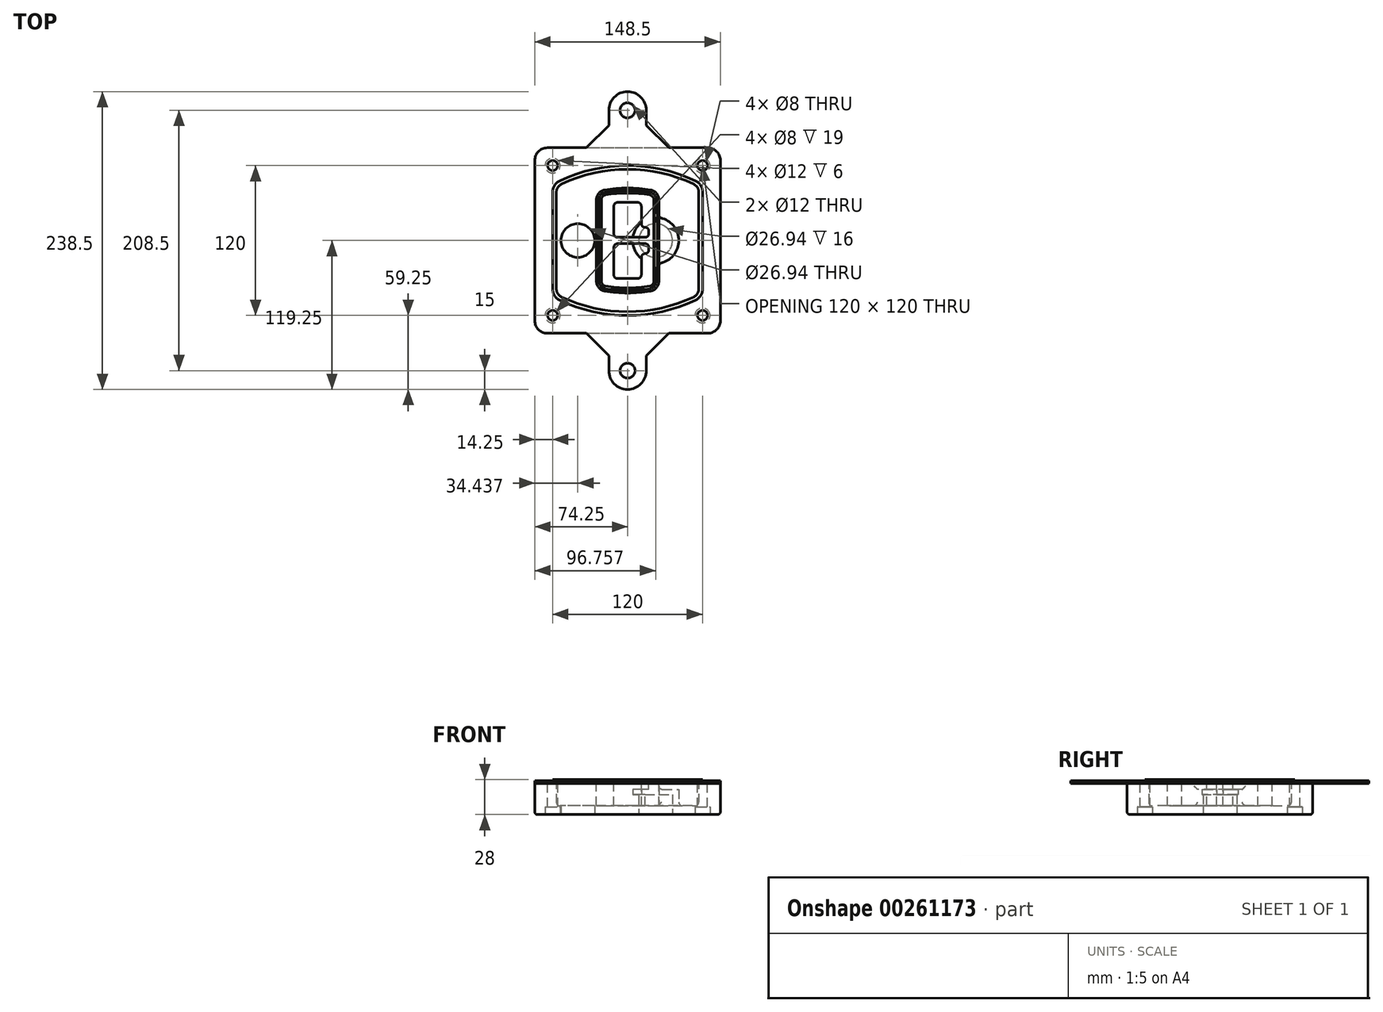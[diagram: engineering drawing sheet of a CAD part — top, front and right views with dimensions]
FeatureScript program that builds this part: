
annotation { "Feature Type Name" : "Feature", "Feature Type Description" : "" }
export const myFeature = defineFeature(function(context is Context, id is Id, definition is map)
    precondition{}
    {
        {
            var Q0;
            Q0=qCreatedBy(makeId("Top.planeOp"),FACE);
            var sketch = newSketch(context, id + "F0", { "sketchPlane" : qUnion([Q0])});
            skPoint(sketch, "E0.rect.middle", {"position": v(0, 0) * mm});
            skLineSegment(sketch, "E1.bottom", {"start": v(-64.25, -74.25) * mm, "end": v(64.25, -74.25) * mm});
            skLineSegment(sketch, "E1.top", {"start": v(-64.25, 74.25) * mm, "end": v(64.25, 74.25) * mm});
            skLineSegment(sketch, "E1.left", {"start": v(-74.25, -64.25) * mm, "end": v(-74.25, 64.25) * mm});
            skLineSegment(sketch, "E1.right", {"start": v(74.25, -64.25) * mm, "end": v(74.25, 64.25) * mm});
            skLineSegment(sketch, "E2", {"start": v(-74.25, 74.25) * mm, "end": v(74.25, -74.25) * mm, "construction": true});
            skLineSegment(sketch, "E3", {"start": v(74.25, 74.25) * mm, "end": v(-74.25, -74.25) * mm, "construction": true});
            skCircle(sketch, "E4", {"center": v(-60, 60) * mm, "radius": 4 * mm});
            skCircle(sketch, "E5", {"center": v(60, 60) * mm, "radius": 4 * mm});
            skCircle(sketch, "E6", {"center": v(60, -60) * mm, "radius": 4 * mm});
            skCircle(sketch, "E7", {"center": v(-60, -60) * mm, "radius": 4 * mm});
            skLineSegment(sketch, "E8", {"start": v(-60, 60) * mm, "end": v(60, 60) * mm, "construction": true});
            skLineSegment(sketch, "E9", {"start": v(60, 60) * mm, "end": v(60, -60) * mm, "construction": true});
            skLineSegment(sketch, "E10", {"start": v(60, -60) * mm, "end": v(-60, -60) * mm, "construction": true});
            skLineSegment(sketch, "E11", {"start": v(-60, -60) * mm, "end": v(-60, 60) * mm, "construction": true});
            skLineSegment(sketch, "E12", {"start": v(-60, 38.83) * mm, "end": v(-60, -38.83) * mm});
            skLineSegment(sketch, "E13", {"start": v(60, 38.83) * mm, "end": v(60, -38.83) * mm});
            skArc(sketch, "E14", {"start": v(54.26, 47.88) * mm, "mid": v(0, 60) * mm, "end": v(-54.26, 47.88) * mm});
            skArc(sketch, "E15", {"start": v(-54.26, -47.88) * mm, "mid": v(0, -60) * mm, "end": v(54.26, -47.88) * mm});
            skLineSegment(sketch, "E16", {"start": v(-60, 0) * mm, "end": v(60, 0) * mm, "construction": true});
            skPoint(sketch, "E17.visualSharp", {"position": v(-60, -45) * mm});
            skArc(sketch, "E17.filletArc", {"start": v(-60, -38.83) * mm, "mid": v(-58.44, -44.2) * mm, "end": v(-54.26, -47.88) * mm});
            skPoint(sketch, "E18.visualSharp", {"position": v(-60, 45) * mm});
            skArc(sketch, "E18.filletArc", {"start": v(-54.26, 47.88) * mm, "mid": v(-58.44, 44.2) * mm, "end": v(-60, 38.83) * mm});
            skPoint(sketch, "E19.visualSharp", {"position": v(60, 45) * mm});
            skArc(sketch, "E19.filletArc", {"start": v(60, 38.83) * mm, "mid": v(58.44, 44.2) * mm, "end": v(54.26, 47.88) * mm});
            skPoint(sketch, "E20.visualSharp", {"position": v(60, -45) * mm});
            skArc(sketch, "E20.filletArc", {"start": v(54.26, -47.88) * mm, "mid": v(58.44, -44.2) * mm, "end": v(60, -38.83) * mm});
            skPoint(sketch, "E21.visualSharp", {"position": v(-74.25, 74.25) * mm});
            skArc(sketch, "E21.filletArc", {"start": v(-64.25, 74.25) * mm, "mid": v(-71.32, 71.32) * mm, "end": v(-74.25, 64.25) * mm});
            skPoint(sketch, "E22.visualSharp", {"position": v(74.25, 74.25) * mm});
            skArc(sketch, "E22.filletArc", {"start": v(74.25, 64.25) * mm, "mid": v(71.32, 71.32) * mm, "end": v(64.25, 74.25) * mm});
            skPoint(sketch, "E23.visualSharp", {"position": v(74.25, -74.25) * mm});
            skArc(sketch, "E23.filletArc", {"start": v(64.25, -74.25) * mm, "mid": v(71.32, -71.32) * mm, "end": v(74.25, -64.25) * mm});
            skPoint(sketch, "E24.visualSharp", {"position": v(-74.25, -74.25) * mm});
            skArc(sketch, "E24.filletArc", {"start": v(-74.25, -64.25) * mm, "mid": v(-71.32, -71.32) * mm, "end": v(-64.25, -74.25) * mm});
            skArc(sketch, "E25.0", {"start": v(57, 38.83) * mm, "mid": v(55.9, 42.58) * mm, "end": v(52.98, 45.17) * mm});
            skLineSegment(sketch, "E25.1", {"start": v(57, 38.83) * mm, "end": v(57, -38.83) * mm});
            skArc(sketch, "E25.2", {"start": v(52.98, -45.17) * mm, "mid": v(55.9, -42.58) * mm, "end": v(57, -38.83) * mm});
            skArc(sketch, "E25.3", {"start": v(-52.98, -45.17) * mm, "mid": v(0, -57) * mm, "end": v(52.98, -45.17) * mm});
            skArc(sketch, "E25.4", {"start": v(-57, -38.83) * mm, "mid": v(-55.9, -42.58) * mm, "end": v(-52.98, -45.17) * mm});
            skArc(sketch, "E25.5", {"start": v(52.98, 45.17) * mm, "mid": v(0, 57) * mm, "end": v(-52.98, 45.17) * mm});
            skLineSegment(sketch, "E25.6", {"start": v(-57, 38.83) * mm, "end": v(-57, -38.83) * mm});
            skArc(sketch, "E25.7", {"start": v(-52.98, 45.17) * mm, "mid": v(-55.9, 42.58) * mm, "end": v(-57, 38.83) * mm});
            skArc(sketch, "E26.0", {"start": v(-55.96, 51.5) * mm, "mid": v(-61.82, 46.33) * mm, "end": v(-64, 38.83) * mm});
            skArc(sketch, "E26.1", {"start": v(55.96, 51.5) * mm, "mid": v(0, 64) * mm, "end": v(-55.96, 51.5) * mm});
            skArc(sketch, "E26.2", {"start": v(64, 38.83) * mm, "mid": v(61.82, 46.33) * mm, "end": v(55.96, 51.5) * mm});
            skLineSegment(sketch, "E26.3", {"start": v(64, 38.83) * mm, "end": v(64, -38.83) * mm});
            skArc(sketch, "E26.4", {"start": v(55.96, -51.5) * mm, "mid": v(61.82, -46.33) * mm, "end": v(64, -38.83) * mm});
            skLineSegment(sketch, "E26.5", {"start": v(-64, 38.83) * mm, "end": v(-64, -38.83) * mm});
            skArc(sketch, "E26.6", {"start": v(-55.96, -51.5) * mm, "mid": v(0, -64) * mm, "end": v(55.96, -51.5) * mm});
            skArc(sketch, "E26.7", {"start": v(-64, -38.83) * mm, "mid": v(-61.82, -46.33) * mm, "end": v(-55.96, -51.5) * mm});
            skSolve(sketch);
        }
        {
            var Q0;
            Q0=makeQuery(id+"F0.imprint","IMPRINT",FACE,{"disambiguationData":[TD([[makeQuery(id+"F0.imprint","IMPRINT",EDGE,{"derivedFrom":sQuery(id+"F0.wireOp",EDGE,"E1.bottom")}),1.0]])]});
            var Q1;
            Q1=makeQuery(id+"F0.imprint","IMPRINT",FACE,{"disambiguationData":[TD([[makeQuery(id+"F0.imprint","IMPRINT",EDGE,{"derivedFrom":sQuery(id+"F0.wireOp",EDGE,"E12")}),1.0]])]});
            var Q2;
            Q2=makeQuery(id+"F0.imprint","IMPRINT",FACE,{"disambiguationData":[TD([[makeQuery(id+"F0.imprint","IMPRINT",EDGE,{"derivedFrom":sQuery(id+"F0.wireOp",EDGE,"E25.0")}),1.0]])]});
            var Q3;
            Q3=makeQuery(id+"F0.imprint","IMPRINT",FACE,{"disambiguationData":[TD([[makeQuery(id+"F0.imprint","IMPRINT",EDGE,{"derivedFrom":sQuery(id+"F0.wireOp",EDGE,"E12")}),-1.0]])]});
            extrude(context, id + "F1", {"entities" : qUnion([Q0, Q1, Q2, Q3]), "oppositeDirection" : true, "depth" : 25 * mm});
        }
        {
            var Q0;
            Q0=makeQuery(id+"F0.imprint","IMPRINT",FACE,{"disambiguationData":[TD([[makeQuery(id+"F0.imprint","IMPRINT",EDGE,{"derivedFrom":sQuery(id+"F0.wireOp",EDGE,"E12")}),1.0]])]});
            extrude(context, id + "F2", {"entities" : qUnion([Q0]), "operationType" : NewBodyOperationType.ADD, "depth" : 3 * mm});
        }
        {
            var Q0;
            Q0=makeQuery(id+"F0.imprint","IMPRINT",FACE,{"disambiguationData":[TD([[makeQuery(id+"F0.imprint","IMPRINT",EDGE,{"derivedFrom":sQuery(id+"F0.wireOp",EDGE,"E25.0")}),1.0]])]});
            extrude(context, id + "F3", {"entities" : qUnion([Q0]), "operationType" : NewBodyOperationType.REMOVE, "oppositeDirection" : true, "depth" : 18 * mm});
        }
        {
            var Q0;
            Q0=makeQuery(id+"F2.opExtrude","CAP_FACE",FACE,{"disambiguationData":[OSD([sQuery(id+"F0.wireOp",EDGE,"E12"),sQuery(id+"F0.wireOp",EDGE,"E13"),sQuery(id+"F0.wireOp",EDGE,"E14"),sQuery(id+"F0.wireOp",EDGE,"E15"),sQuery(id+"F0.wireOp",EDGE,"E17.filletArc"),sQuery(id+"F0.wireOp",EDGE,"E18.filletArc"),sQuery(id+"F0.wireOp",EDGE,"E19.filletArc"),sQuery(id+"F0.wireOp",EDGE,"E20.filletArc"),sQuery(id+"F0.wireOp",EDGE,"E25.0"),sQuery(id+"F0.wireOp",EDGE,"E25.1"),sQuery(id+"F0.wireOp",EDGE,"E25.2"),sQuery(id+"F0.wireOp",EDGE,"E25.3"),sQuery(id+"F0.wireOp",EDGE,"E25.4"),sQuery(id+"F0.wireOp",EDGE,"E25.5"),sQuery(id+"F0.wireOp",EDGE,"E25.6"),sQuery(id+"F0.wireOp",EDGE,"E25.7")])],"isStart":false});
            var sketch = newSketch(context, id + "F4", { "sketchPlane" : qUnion([Q0])});
            skArc(sketch, "E27.0", {"start": v(-18.34, -40.45) * mm, "mid": v(0, -42) * mm, "end": v(18.34, -40.45) * mm});
            skArc(sketch, "E28.0", {"start": v(18.34, 40.45) * mm, "mid": v(0, 42) * mm, "end": v(-18.34, 40.45) * mm});
            skLineSegment(sketch, "E29", {"start": v(-25, 32.57) * mm, "end": v(-25, -32.57) * mm});
            skLineSegment(sketch, "E30", {"start": v(25, 32.57) * mm, "end": v(25, -32.57) * mm});
            skLineSegment(sketch, "E31", {"start": v(-25, 39.1) * mm, "end": v(25, 39.1) * mm, "construction": true});
            skLineSegment(sketch, "E32", {"start": v(-25, -39.1) * mm, "end": v(25, -39.1) * mm, "construction": true});
            skPoint(sketch, "E33.visualSharp", {"position": v(-25, 39.1) * mm});
            skArc(sketch, "E33.filletArc", {"start": v(-18.34, 40.45) * mm, "mid": v(-23.11, 37.73) * mm, "end": v(-25, 32.57) * mm});
            skPoint(sketch, "E34.visualSharp", {"position": v(25, 39.1) * mm});
            skArc(sketch, "E34.filletArc", {"start": v(25, 32.57) * mm, "mid": v(23.11, 37.73) * mm, "end": v(18.34, 40.45) * mm});
            skPoint(sketch, "E35.visualSharp", {"position": v(25, -39.1) * mm});
            skArc(sketch, "E35.filletArc", {"start": v(18.34, -40.45) * mm, "mid": v(23.11, -37.73) * mm, "end": v(25, -32.57) * mm});
            skPoint(sketch, "E36.visualSharp", {"position": v(-25, -39.1) * mm});
            skArc(sketch, "E36.filletArc", {"start": v(-25, -32.57) * mm, "mid": v(-23.11, -37.73) * mm, "end": v(-18.34, -40.45) * mm});
            skArc(sketch, "E37.0", {"start": v(52.98, 45.17) * mm, "mid": v(0, 57) * mm, "end": v(-52.98, 45.17) * mm});
            skArc(sketch, "E37.1", {"start": v(-52.98, 45.17) * mm, "mid": v(-55.9, 42.58) * mm, "end": v(-57, 38.83) * mm});
            skLineSegment(sketch, "E37.2", {"start": v(-57, 38.83) * mm, "end": v(-57, -38.83) * mm});
            skArc(sketch, "E37.3", {"start": v(-57, -38.83) * mm, "mid": v(-55.9, -42.58) * mm, "end": v(-52.98, -45.17) * mm});
            skArc(sketch, "E37.4", {"start": v(-52.98, -45.17) * mm, "mid": v(0, -57) * mm, "end": v(52.98, -45.17) * mm});
            skArc(sketch, "E37.5", {"start": v(52.98, -45.17) * mm, "mid": v(55.9, -42.58) * mm, "end": v(57, -38.83) * mm});
            skLineSegment(sketch, "E37.6", {"start": v(57, 38.83) * mm, "end": v(57, -38.83) * mm});
            skArc(sketch, "E37.7", {"start": v(57, 38.83) * mm, "mid": v(55.9, 42.58) * mm, "end": v(52.98, 45.17) * mm});
            skLineSegment(sketch, "E38.0", {"start": v(23, 32.57) * mm, "end": v(23, -32.57) * mm});
            skArc(sketch, "E38.1", {"start": v(18, -38.48) * mm, "mid": v(21.58, -36.44) * mm, "end": v(23, -32.57) * mm});
            skArc(sketch, "E38.2", {"start": v(-18, -38.48) * mm, "mid": v(0, -40) * mm, "end": v(18, -38.48) * mm});
            skArc(sketch, "E38.3", {"start": v(-23, -32.57) * mm, "mid": v(-21.58, -36.44) * mm, "end": v(-18, -38.48) * mm});
            skLineSegment(sketch, "E38.4", {"start": v(-23, 32.57) * mm, "end": v(-23, -32.57) * mm});
            skArc(sketch, "E38.5", {"start": v(23, 32.57) * mm, "mid": v(21.58, 36.44) * mm, "end": v(18, 38.48) * mm});
            skArc(sketch, "E38.6", {"start": v(-18, 38.48) * mm, "mid": v(-21.58, 36.44) * mm, "end": v(-23, 32.57) * mm});
            skArc(sketch, "E38.7", {"start": v(18, 38.48) * mm, "mid": v(0, 40) * mm, "end": v(-18, 38.48) * mm});
            skArc(sketch, "E39.0", {"start": v(21, 32.57) * mm, "mid": v(20.06, 35.15) * mm, "end": v(17.67, 36.5) * mm});
            skLineSegment(sketch, "E39.1", {"start": v(21, 32.57) * mm, "end": v(21, -32.57) * mm});
            skArc(sketch, "E39.2", {"start": v(17.67, -36.5) * mm, "mid": v(20.06, -35.15) * mm, "end": v(21, -32.57) * mm});
            skArc(sketch, "E39.3", {"start": v(-17.67, -36.5) * mm, "mid": v(0, -38) * mm, "end": v(17.67, -36.5) * mm});
            skArc(sketch, "E39.4", {"start": v(-21, -32.57) * mm, "mid": v(-20.06, -35.15) * mm, "end": v(-17.67, -36.5) * mm});
            skArc(sketch, "E39.5", {"start": v(17.67, 36.5) * mm, "mid": v(0, 38) * mm, "end": v(-17.67, 36.5) * mm});
            skLineSegment(sketch, "E39.6", {"start": v(-21, 32.57) * mm, "end": v(-21, -32.57) * mm});
            skArc(sketch, "E39.7", {"start": v(-17.67, 36.5) * mm, "mid": v(-20.06, 35.15) * mm, "end": v(-21, 32.57) * mm});
            skLineSegment(sketch, "E40", {"start": v(-25, 0) * mm, "end": v(25, 0) * mm, "construction": true});
            skLineSegment(sketch, "E41", {"start": v(-11, 5.5) * mm, "end": v(-11, 27.5) * mm});
            skLineSegment(sketch, "E42", {"start": v(-8, 30.5) * mm, "end": v(8, 30.5) * mm});
            skLineSegment(sketch, "E43", {"start": v(11, 27.5) * mm, "end": v(11, 13.5) * mm});
            skLineSegment(sketch, "E44", {"start": v(14, 10.5) * mm, "end": v(14, 10.5) * mm});
            skLineSegment(sketch, "E45", {"start": v(17, 7.5) * mm, "end": v(17, 5.5) * mm});
            skLineSegment(sketch, "E46", {"start": v(14, 2.5) * mm, "end": v(-8, 2.5) * mm});
            skPoint(sketch, "E47.visualSharp", {"position": v(-11, 30.5) * mm});
            skArc(sketch, "E47.filletArc", {"start": v(-8, 30.5) * mm, "mid": v(-10.12, 29.62) * mm, "end": v(-11, 27.5) * mm});
            skPoint(sketch, "E48.visualSharp", {"position": v(11, 30.5) * mm});
            skArc(sketch, "E48.filletArc", {"start": v(11, 27.5) * mm, "mid": v(10.12, 29.62) * mm, "end": v(8, 30.5) * mm});
            skPoint(sketch, "E49.visualSharp", {"position": v(11, 10.5) * mm});
            skArc(sketch, "E49.filletArc", {"start": v(11, 13.5) * mm, "mid": v(11.88, 11.38) * mm, "end": v(14, 10.5) * mm});
            skPoint(sketch, "E50.visualSharp", {"position": v(17, 10.5) * mm});
            skArc(sketch, "E50.filletArc", {"start": v(17, 7.5) * mm, "mid": v(16.12, 9.62) * mm, "end": v(14, 10.5) * mm});
            skPoint(sketch, "E51.visualSharp", {"position": v(17, 2.5) * mm});
            skArc(sketch, "E51.filletArc", {"start": v(14, 2.5) * mm, "mid": v(16.12, 3.38) * mm, "end": v(17, 5.5) * mm});
            skPoint(sketch, "E52.visualSharp", {"position": v(-11, 2.5) * mm});
            skArc(sketch, "E52.filletArc", {"start": v(-11, 5.5) * mm, "mid": v(-10.12, 3.38) * mm, "end": v(-8, 2.5) * mm});
            skLineSegment(sketch, "E53.0.MirrorCS", {"start": v(14, -2.5) * mm, "end": v(-8, -2.5) * mm});
            skArc(sketch, "E54.0.MirrorCS", {"start": v(-11, -5.5) * mm, "mid": v(-10.12, -3.38) * mm, "end": v(-8, -2.5) * mm});
            skLineSegment(sketch, "E55.0.MirrorCS", {"start": v(-11, -5.5) * mm, "end": v(-11, -27.5) * mm});
            skArc(sketch, "E56.0.MirrorCS", {"start": v(-8, -30.5) * mm, "mid": v(-10.12, -29.62) * mm, "end": v(-11, -27.5) * mm});
            skLineSegment(sketch, "E57.0.MirrorCS", {"start": v(-8, -30.5) * mm, "end": v(8, -30.5) * mm});
            skArc(sketch, "E58.0.MirrorCS", {"start": v(11, -27.5) * mm, "mid": v(10.12, -29.62) * mm, "end": v(8, -30.5) * mm});
            skLineSegment(sketch, "E59.0.MirrorCS", {"start": v(11, -27.5) * mm, "end": v(11, -13.5) * mm});
            skArc(sketch, "E60.0.MirrorCS", {"start": v(11, -13.5) * mm, "mid": v(11.88, -11.38) * mm, "end": v(14, -10.5) * mm});
            skArc(sketch, "E61.0.MirrorCS", {"start": v(17, -7.5) * mm, "mid": v(16.12, -9.62) * mm, "end": v(14, -10.5) * mm});
            skLineSegment(sketch, "E62.0.MirrorCS", {"start": v(17, -7.5) * mm, "end": v(17, -5.5) * mm});
            skArc(sketch, "E63.0.MirrorCS", {"start": v(14, -2.5) * mm, "mid": v(16.12, -3.38) * mm, "end": v(17, -5.5) * mm});
            skSolve(sketch);
        }
        {
            var Q0;
            Q0=makeQuery(id+"F4.imprint","IMPRINT",FACE,{"disambiguationData":[TD([[makeQuery(id+"F4.imprint","IMPRINT",EDGE,{"derivedFrom":sQuery(id+"F4.wireOp",EDGE,"E27.0")}),1.0]])]});
            var Q1;
            Q1=makeQuery(id+"F4.imprint","IMPRINT",FACE,{"disambiguationData":[TD([[makeQuery(id+"F4.imprint","IMPRINT",EDGE,{"derivedFrom":sQuery(id+"F4.wireOp",EDGE,"E38.0")}),-1.0]])]});
            var Q2;
            Q2=makeQuery(id+"F4.imprint","IMPRINT",FACE,{"disambiguationData":[TD([[makeQuery(id+"F4.imprint","IMPRINT",EDGE,{"derivedFrom":sQuery(id+"F4.wireOp",EDGE,"E39.0")}),1.0]])]});
            extrude(context, id + "F5", {"entities" : qUnion([Q0, Q1, Q2]), "operationType" : NewBodyOperationType.ADD, "endBound" : BoundingType.UP_TO_NEXT, "oppositeDirection" : true, "depth" : 25 * mm});
        }
        {
            var Q0;
            Q0=makeQuery(id+"F4.imprint","IMPRINT",FACE,{"disambiguationData":[TD([[makeQuery(id+"F4.imprint","IMPRINT",EDGE,{"derivedFrom":sQuery(id+"F4.wireOp",EDGE,"E38.0")}),-1.0]])]});
            extrude(context, id + "F6", {"entities" : qUnion([Q0]), "operationType" : NewBodyOperationType.REMOVE, "oppositeDirection" : true, "depth" : 2 * mm});
        }
        {
            var Q0;
            Q0=makeQuery(id+"F1.opExtrude","CAP_FACE",FACE,{"disambiguationData":[OSD([sQuery(id+"F0.wireOp",EDGE,"E1.bottom"),sQuery(id+"F0.wireOp",EDGE,"E1.top"),sQuery(id+"F0.wireOp",EDGE,"E1.left"),sQuery(id+"F0.wireOp",EDGE,"E1.right"),sQuery(id+"F0.wireOp",EDGE,"E4"),sQuery(id+"F0.wireOp",EDGE,"E5"),sQuery(id+"F0.wireOp",EDGE,"E6"),sQuery(id+"F0.wireOp",EDGE,"E7"),sQuery(id+"F0.wireOp",EDGE,"E21.filletArc"),sQuery(id+"F0.wireOp",EDGE,"E22.filletArc"),sQuery(id+"F0.wireOp",EDGE,"E23.filletArc"),sQuery(id+"F0.wireOp",EDGE,"E24.filletArc")])],"isStart":false});
            var sketch = newSketch(context, id + "F7", { "sketchPlane" : qUnion([Q0])});
            skCircle(sketch, "E64", {"center": v(22.5, 0) * mm, "radius": 13.47 * mm});
            skCircle(sketch, "E65", {"center": v(-39.81, 0) * mm, "radius": 13.47 * mm});
            skLineSegment(sketch, "E66", {"start": v(74.25, 0) * mm, "end": v(-74.25, 0) * mm});
            skCircle(sketch, "E67", {"center": v(22.5, 0) * mm, "radius": 18.47 * mm});
            skCircle(sketch, "E68", {"center": v(60, -60) * mm, "radius": 6 * mm});
            skCircle(sketch, "E69", {"center": v(-60, -60) * mm, "radius": 6 * mm});
            skCircle(sketch, "E70", {"center": v(-60, 60) * mm, "radius": 6 * mm});
            skCircle(sketch, "E71", {"center": v(60, 60) * mm, "radius": 6 * mm});
            skSolve(sketch);
        }
        {
            var Q0;
            {var subQ1=sQuery(id+"F7.wireOp",EDGE,"E66");var subQ4=sQuery(id+"F7.wireOp",EDGE,"E64");var subQ6=makeQuery(id+"F7.imprint","INTERSECT",VERTEX,{"disambiguationData":[OD(0.0)],"derivedFrom":[subQ4,subQ1]});Q0=makeQuery(id+"F7.imprint","IMPRINT",FACE,{"disambiguationData":[TD([[makeQuery(id+"F7.imprint","IMPRINT",EDGE,{"disambiguationData":[TD([[subQ6,-1.0]])],"derivedFrom":subQ4}),-1.0]])]});}
            var Q1;
            {var subQ0=sQuery(id+"F7.wireOp",EDGE,"E66");var subQ1=sQuery(id+"F7.wireOp",EDGE,"E64");var subQ3=makeQuery(id+"F7.imprint","INTERSECT",VERTEX,{"disambiguationData":[OD(0.0)],"derivedFrom":[subQ1,subQ0]});Q1=makeQuery(id+"F7.imprint","IMPRINT",FACE,{"disambiguationData":[TD([[makeQuery(id+"F7.imprint","IMPRINT",EDGE,{"disambiguationData":[TD([[subQ3,-1.0]])],"derivedFrom":subQ1}),1.0]])]});}
            var Q2;
            {var subQ0=sQuery(id+"F7.wireOp",EDGE,"E66");var subQ1=sQuery(id+"F7.wireOp",EDGE,"E64");var subQ3=makeQuery(id+"F7.imprint","INTERSECT",VERTEX,{"disambiguationData":[OD(0.0)],"derivedFrom":[subQ1,subQ0]});Q2=makeQuery(id+"F7.imprint","IMPRINT",FACE,{"disambiguationData":[TD([[makeQuery(id+"F7.imprint","IMPRINT",EDGE,{"disambiguationData":[TD([[subQ3,1.0]])],"derivedFrom":subQ1}),1.0]])]});}
            var Q3;
            {var subQ1=sQuery(id+"F7.wireOp",EDGE,"E66");var subQ4=sQuery(id+"F7.wireOp",EDGE,"E64");var subQ6=makeQuery(id+"F7.imprint","INTERSECT",VERTEX,{"disambiguationData":[OD(0.0)],"derivedFrom":[subQ4,subQ1]});Q3=makeQuery(id+"F7.imprint","IMPRINT",FACE,{"disambiguationData":[TD([[makeQuery(id+"F7.imprint","IMPRINT",EDGE,{"disambiguationData":[TD([[subQ6,1.0]])],"derivedFrom":subQ4}),-1.0]])]});}
            extrude(context, id + "F8", {"entities" : qUnion([Q0, Q1, Q2, Q3]), "operationType" : NewBodyOperationType.ADD, "oppositeDirection" : true, "depth" : 20 * mm});
        }
        {
            var Q0;
            {var subQ0=sQuery(id+"F7.wireOp",EDGE,"E66");var subQ1=sQuery(id+"F7.wireOp",EDGE,"E64");var subQ3=makeQuery(id+"F7.imprint","INTERSECT",VERTEX,{"disambiguationData":[OD(0.0)],"derivedFrom":[subQ1,subQ0]});Q0=makeQuery(id+"F7.imprint","IMPRINT",FACE,{"disambiguationData":[TD([[makeQuery(id+"F7.imprint","IMPRINT",EDGE,{"disambiguationData":[TD([[subQ3,-1.0]])],"derivedFrom":subQ1}),1.0]])]});}
            var Q1;
            {var subQ0=sQuery(id+"F7.wireOp",EDGE,"E66");var subQ1=sQuery(id+"F7.wireOp",EDGE,"E64");var subQ3=makeQuery(id+"F7.imprint","INTERSECT",VERTEX,{"disambiguationData":[OD(0.0)],"derivedFrom":[subQ1,subQ0]});Q1=makeQuery(id+"F7.imprint","IMPRINT",FACE,{"disambiguationData":[TD([[makeQuery(id+"F7.imprint","IMPRINT",EDGE,{"disambiguationData":[TD([[subQ3,1.0]])],"derivedFrom":subQ1}),1.0]])]});}
            extrude(context, id + "F9", {"entities" : qUnion([Q0, Q1]), "operationType" : NewBodyOperationType.REMOVE, "oppositeDirection" : true, "depth" : 16 * mm});
        }
        {
            var Q0;
            {var subQ0=sQuery(id+"F7.wireOp",EDGE,"E66");var subQ1=sQuery(id+"F7.wireOp",EDGE,"E65");var subQ3=makeQuery(id+"F7.imprint","INTERSECT",VERTEX,{"disambiguationData":[OD(0.0)],"derivedFrom":[subQ1,subQ0]});Q0=makeQuery(id+"F7.imprint","IMPRINT",FACE,{"disambiguationData":[TD([[makeQuery(id+"F7.imprint","IMPRINT",EDGE,{"disambiguationData":[TD([[subQ3,-1.0]])],"derivedFrom":subQ1}),1.0]])]});}
            var Q1;
            {var subQ0=sQuery(id+"F7.wireOp",EDGE,"E66");var subQ1=sQuery(id+"F7.wireOp",EDGE,"E65");var subQ3=makeQuery(id+"F7.imprint","INTERSECT",VERTEX,{"disambiguationData":[OD(0.0)],"derivedFrom":[subQ1,subQ0]});Q1=makeQuery(id+"F7.imprint","IMPRINT",FACE,{"disambiguationData":[TD([[makeQuery(id+"F7.imprint","IMPRINT",EDGE,{"disambiguationData":[TD([[subQ3,1.0]])],"derivedFrom":subQ1}),1.0]])]});}
            extrude(context, id + "F10", {"entities" : qUnion([Q0, Q1]), "operationType" : NewBodyOperationType.REMOVE, "oppositeDirection" : true, "depth" : 25 * mm});
        }
        {
            var Q0;
            Q0=makeQuery(id+"F7.imprint","IMPRINT",FACE,{"disambiguationData":[TD([[makeQuery(id+"F7.imprint","IMPRINT",EDGE,{"derivedFrom":sQuery(id+"F7.wireOp",EDGE,"E68")}),1.0]])]});
            var Q1;
            Q1=makeQuery(id+"F7.imprint","IMPRINT",FACE,{"disambiguationData":[TD([[makeQuery(id+"F7.imprint","IMPRINT",EDGE,{"derivedFrom":makeQuery(id+"F1.opExtrude","CAP_EDGE",EDGE,{"disambiguationData":[OSD([sQuery(id+"F0.wireOp",EDGE,"E5")])],"isStart":false})}),-1.0]])]});
            var Q2;
            Q2=makeQuery(id+"F7.imprint","IMPRINT",FACE,{"disambiguationData":[TD([[makeQuery(id+"F7.imprint","IMPRINT",EDGE,{"derivedFrom":sQuery(id+"F7.wireOp",EDGE,"E69")}),1.0]])]});
            var Q3;
            Q3=makeQuery(id+"F7.imprint","IMPRINT",FACE,{"disambiguationData":[TD([[makeQuery(id+"F7.imprint","IMPRINT",EDGE,{"derivedFrom":makeQuery(id+"F1.opExtrude","CAP_EDGE",EDGE,{"disambiguationData":[OSD([sQuery(id+"F0.wireOp",EDGE,"E4")])],"isStart":false})}),-1.0]])]});
            var Q4;
            Q4=makeQuery(id+"F7.imprint","IMPRINT",FACE,{"disambiguationData":[TD([[makeQuery(id+"F7.imprint","IMPRINT",EDGE,{"derivedFrom":sQuery(id+"F7.wireOp",EDGE,"E70")}),1.0]])]});
            var Q5;
            Q5=makeQuery(id+"F7.imprint","IMPRINT",FACE,{"disambiguationData":[TD([[makeQuery(id+"F7.imprint","IMPRINT",EDGE,{"derivedFrom":makeQuery(id+"F1.opExtrude","CAP_EDGE",EDGE,{"disambiguationData":[OSD([sQuery(id+"F0.wireOp",EDGE,"E7")])],"isStart":false})}),-1.0]])]});
            var Q6;
            Q6=makeQuery(id+"F7.imprint","IMPRINT",FACE,{"disambiguationData":[TD([[makeQuery(id+"F7.imprint","IMPRINT",EDGE,{"derivedFrom":sQuery(id+"F7.wireOp",EDGE,"E71")}),1.0]])]});
            var Q7;
            Q7=makeQuery(id+"F7.imprint","IMPRINT",FACE,{"disambiguationData":[TD([[makeQuery(id+"F7.imprint","IMPRINT",EDGE,{"derivedFrom":makeQuery(id+"F1.opExtrude","CAP_EDGE",EDGE,{"disambiguationData":[OSD([sQuery(id+"F0.wireOp",EDGE,"E6")])],"isStart":false})}),-1.0]])]});
            extrude(context, id + "F11", {"entities" : qUnion([Q0, Q1, Q2, Q3, Q4, Q5, Q6, Q7]), "operationType" : NewBodyOperationType.REMOVE, "oppositeDirection" : true, "depth" : 6 * mm});
        }
        {
            var Q0;
            Q0=makeQuery(id+"F9.boolean.opBoolean","COPY",FACE,{"derivedFrom":makeQuery(id+"F9.opExtrude","CAP_FACE",FACE,{"disambiguationData":[OSD([sQuery(id+"F7.wireOp",EDGE,"E64")])],"isStart":false})});
            var sketch = newSketch(context, id + "F12", { "sketchPlane" : qUnion([Q0])});
            skArc(sketch, "E72.0", {"start": v(11, 14.45) * mm, "mid": v(6.45, 9.13) * mm, "end": v(4.2, 2.5) * mm});
            skArc(sketch, "E72.1", {"start": v(4.2, -2.5) * mm, "mid": v(6.45, -9.13) * mm, "end": v(11, -14.45) * mm});
            skLineSegment(sketch, "E73", {"start": v(4.2, -2.5) * mm, "end": v(14, -2.5) * mm});
            skLineSegment(sketch, "E74.0", {"start": v(14, 2.5) * mm, "end": v(4.2, 2.5) * mm});
            skArc(sketch, "E74.1", {"start": v(14, 2.5) * mm, "mid": v(16.12, 3.38) * mm, "end": v(17, 5.5) * mm});
            skLineSegment(sketch, "E74.2", {"start": v(17, 7.5) * mm, "end": v(17, 5.5) * mm});
            skArc(sketch, "E74.3", {"start": v(17, 7.5) * mm, "mid": v(16.12, 9.62) * mm, "end": v(14, 10.5) * mm});
            skArc(sketch, "E74.4", {"start": v(11, 13.5) * mm, "mid": v(11.88, 11.38) * mm, "end": v(14, 10.5) * mm});
            skLineSegment(sketch, "E74.5", {"start": v(11, 14.45) * mm, "end": v(11, 13.5) * mm});
            skLineSegment(sketch, "E74.7", {"start": v(14, -2.5) * mm, "end": v(4.2, -2.5) * mm});
            skArc(sketch, "E74.8", {"start": v(14, -2.5) * mm, "mid": v(16.12, -3.38) * mm, "end": v(17, -5.5) * mm});
            skLineSegment(sketch, "E74.9", {"start": v(17, -7.5) * mm, "end": v(17, -5.5) * mm});
            skArc(sketch, "E74.10", {"start": v(17, -7.5) * mm, "mid": v(16.12, -9.62) * mm, "end": v(14, -10.5) * mm});
            skArc(sketch, "E74.11", {"start": v(11, -13.5) * mm, "mid": v(11.88, -11.38) * mm, "end": v(14, -10.5) * mm});
            skLineSegment(sketch, "E74.12", {"start": v(11, -14.45) * mm, "end": v(11, -13.5) * mm});
            skPoint(sketch, "E75.orphan", {"position": v(11, -27.5) * mm});
            skPoint(sketch, "E76.orphan", {"position": v(-8, -2.5) * mm});
            skPoint(sketch, "E77.orphan", {"position": v(-8, 2.5) * mm});
            skPoint(sketch, "E78.orphan", {"position": v(11, 27.5) * mm});
            skSolve(sketch);
        }
        {
            var Q0;
            {var subQ7=sQuery(id+"F12.wireOp",EDGE,"E72.0");var subQ14=sQuery(id+"F12.wireOp",EDGE,"E72.1");var subQ16=sQuery(id+"F12.wireOp",EDGE,"E74.1");var subQ18=sQuery(id+"F12.wireOp",EDGE,"E74.8");Q0=qUnion([makeQuery(id+"F12.imprint","IMPRINT",FACE,{"disambiguationData":[TD([[makeQuery(id+"F12.imprint","IMPRINT",EDGE,{"derivedFrom":subQ7}),1.0]])]}),makeQuery(id+"F12.imprint","IMPRINT",FACE,{"disambiguationData":[TD([[makeQuery(id+"F12.imprint","IMPRINT",EDGE,{"derivedFrom":subQ14}),1.0]])]}),makeQuery(id+"F12.imprint","IMPRINT",FACE,{"disambiguationData":[TD([[makeQuery(id+"F12.imprint","IMPRINT",EDGE,{"derivedFrom":subQ16}),1.0]])]}),makeQuery(id+"F12.imprint","IMPRINT",FACE,{"disambiguationData":[TD([[makeQuery(id+"F12.imprint","IMPRINT",EDGE,{"derivedFrom":subQ18}),-1.0]])]})]);}
            var Q1;
            Q1=makeQuery(id+"F5.boolean.opBoolean","SPLIT",FACE,{"disambiguationData":[TD([makeQuery(id+"F5.opExtrude","SWEPT_FACE",FACE,{"disambiguationData":[OSD([sQuery(id+"F4.wireOp",EDGE,"E41")])]})])],"derivedFrom":makeQuery(id+"F3.boolean.opBoolean","COPY",FACE,{"derivedFrom":makeQuery(id+"F3.opExtrude","CAP_FACE",FACE,{"disambiguationData":[OSD([sQuery(id+"F0.wireOp",EDGE,"E25.0"),sQuery(id+"F0.wireOp",EDGE,"E25.1"),sQuery(id+"F0.wireOp",EDGE,"E25.2"),sQuery(id+"F0.wireOp",EDGE,"E25.3"),sQuery(id+"F0.wireOp",EDGE,"E25.4"),sQuery(id+"F0.wireOp",EDGE,"E25.5"),sQuery(id+"F0.wireOp",EDGE,"E25.6"),sQuery(id+"F0.wireOp",EDGE,"E25.7")])],"isStart":false})})});
            extrude(context, id + "F13", {"entities" : qUnion([Q0]), "operationType" : NewBodyOperationType.REMOVE, "endBound" : BoundingType.UP_TO_SURFACE, "endBoundEntityFace" : qUnion([Q1]), "depth" : 25 * mm});
        }
        {
            var Q0;
            Q0=makeQuery(id+"F3.boolean.opBoolean","COPY",EDGE,{"derivedFrom":makeQuery(id+"F3.opExtrude","CAP_EDGE",EDGE,{"disambiguationData":[OSD([sQuery(id+"F0.wireOp",EDGE,"E25.6")])],"isStart":false})});
            var Q1;
            Q1=makeQuery(id+"F8.boolean.opBoolean","INTERSECT",EDGE,{"derivedFrom":[makeQuery(id+"F5.opExtrude","SWEPT_FACE",FACE,{"disambiguationData":[OSD([sQuery(id+"F4.wireOp",EDGE,"E30")])]}),makeQuery(id+"F8.opExtrude","CAP_FACE",FACE,{"disambiguationData":[OSD([sQuery(id+"F7.wireOp",EDGE,"E67")])],"isStart":false})]});
            var Q2;
            Q2=makeQuery(id+"F8.boolean.opBoolean","INTERSECT",EDGE,{"disambiguationData":[OD(1.0)],"derivedFrom":[makeQuery(id+"F5.opExtrude","SWEPT_FACE",FACE,{"disambiguationData":[OSD([sQuery(id+"F4.wireOp",EDGE,"E30")])]}),makeQuery(id+"F8.opExtrude","SWEPT_FACE",FACE,{"disambiguationData":[OSD([sQuery(id+"F7.wireOp",EDGE,"E67")])]})]});
            var Q3;
            {var subQ0=sQuery(id+"F4.wireOp",EDGE,"E30");Q3=makeQuery(id+"F8.boolean.opBoolean","SPLIT",EDGE,{"disambiguationData":[TD([makeQuery(id+"F5.opExtrude","SWEPT_FACE",FACE,{"disambiguationData":[OSD([sQuery(id+"F4.wireOp",EDGE,"E35.filletArc")])]})])],"derivedFrom":makeQuery(id+"F5.opExtrude","CAP_EDGE",EDGE,{"disambiguationData":[OSD([subQ0])],"isStart":false})});}
            var Q4;
            {var subQ0=sQuery(id+"F0.wireOp",EDGE,"E25.7");var subQ1=sQuery(id+"F0.wireOp",EDGE,"E25.1");var subQ2=sQuery(id+"F0.wireOp",EDGE,"E25.6");var subQ3=sQuery(id+"F0.wireOp",EDGE,"E25.5");var subQ4=sQuery(id+"F0.wireOp",EDGE,"E25.4");var subQ5=sQuery(id+"F0.wireOp",EDGE,"E25.0");var subQ6=sQuery(id+"F0.wireOp",EDGE,"E25.2");var subQ7=sQuery(id+"F0.wireOp",EDGE,"E25.3");Q4=makeQuery(id+"F8.boolean.opBoolean","INTERSECT",EDGE,{"derivedFrom":[makeQuery(id+"F5.boolean.opBoolean","SPLIT",FACE,{"disambiguationData":[TD([makeQuery(id+"F2.opExtrude","SWEPT_FACE",FACE,{"disambiguationData":[OSD([subQ5])]})])],"derivedFrom":makeQuery(id+"F3.boolean.opBoolean","COPY",FACE,{"derivedFrom":makeQuery(id+"F3.opExtrude","CAP_FACE",FACE,{"disambiguationData":[OSD([subQ5,subQ1,subQ6,subQ7,subQ4,subQ3,subQ2,subQ0])],"isStart":false})})}),makeQuery(id+"F8.opExtrude","SWEPT_FACE",FACE,{"disambiguationData":[OSD([sQuery(id+"F7.wireOp",EDGE,"E67")])]})]});}
            var Q5;
            Q5=makeQuery(id+"F8.boolean.opBoolean","INTERSECT",EDGE,{"disambiguationData":[OD(0.0)],"derivedFrom":[makeQuery(id+"F5.opExtrude","SWEPT_FACE",FACE,{"disambiguationData":[OSD([sQuery(id+"F4.wireOp",EDGE,"E30")])]}),makeQuery(id+"F8.opExtrude","SWEPT_FACE",FACE,{"disambiguationData":[OSD([sQuery(id+"F7.wireOp",EDGE,"E67")])]})]});
            fillet(context, id + "F14", {"entities" : qUnion([Q0, Q1, Q2, Q3, Q4, Q5]), "radius" : 3 * mm, "tangentPropagation" : true, "allowEdgeOverflow" : false});
        }
        {
            var Q0;
            Q0=makeQuery(id+"F1.opExtrude","CAP_EDGE",EDGE,{"disambiguationData":[OSD([sQuery(id+"F0.wireOp",EDGE,"E1.bottom")])],"isStart":false});
            fillet(context, id + "F15", {"entities" : qUnion([Q0]), "radius" : 2 * mm, "tangentPropagation" : true, "allowEdgeOverflow" : false});
        }
        {
            var Q0;
            {var subQ0=sQuery(id+"F0.wireOp",EDGE,"E22.filletArc");var subQ1=sQuery(id+"F0.wireOp",EDGE,"E7");var subQ2=sQuery(id+"F0.wireOp",EDGE,"E6");var subQ3=sQuery(id+"F0.wireOp",EDGE,"E5");var subQ4=sQuery(id+"F0.wireOp",EDGE,"E4");var subQ5=sQuery(id+"F0.wireOp",EDGE,"E1.bottom");var subQ6=sQuery(id+"F0.wireOp",EDGE,"E21.filletArc");var subQ7=sQuery(id+"F0.wireOp",EDGE,"E1.top");var subQ8=sQuery(id+"F0.wireOp",EDGE,"E1.left");var subQ9=sQuery(id+"F0.wireOp",EDGE,"E1.right");var subQ10=sQuery(id+"F0.wireOp",EDGE,"E23.filletArc");var subQ11=sQuery(id+"F0.wireOp",EDGE,"E24.filletArc");Q0=makeQuery(id+"F2.boolean.opBoolean","SPLIT",FACE,{"disambiguationData":[TD([makeQuery(id+"F1.opExtrude","SWEPT_FACE",FACE,{"disambiguationData":[OSD([subQ5])]})])],"derivedFrom":makeQuery(id+"F1.opExtrude","CAP_FACE",FACE,{"disambiguationData":[OSD([subQ5,subQ7,subQ8,subQ9,subQ4,subQ3,subQ2,subQ1,subQ6,subQ0,subQ10,subQ11])],"isStart":true})});}
            var sketch = newSketch(context, id + "F16", { "sketchPlane" : qUnion([Q0])});
            skLineSegment(sketch, "E79", {"start": v(0, 74.25) * mm, "end": v(0, 104.25) * mm});
            skCircle(sketch, "E80", {"center": v(0, 104.25) * mm, "radius": 6 * mm});
            skArc(sketch, "E81", {"start": v(15, 104.25) * mm, "mid": v(0, 119.25) * mm, "end": v(-15, 104.25) * mm});
            skLineSegment(sketch, "E82", {"start": v(-15, 104.25) * mm, "end": v(-15, 92.25) * mm});
            skLineSegment(sketch, "E83", {"start": v(15, 104.25) * mm, "end": v(15, 92.25) * mm});
            skLineSegment(sketch, "E84", {"start": v(-33, 74.25) * mm, "end": v(-15, 92.25) * mm});
            skLineSegment(sketch, "E85", {"start": v(33, 74.25) * mm, "end": v(15, 92.25) * mm});
            skLineSegment(sketch, "E86.MirrorCS", {"start": v(0, -74.25) * mm, "end": v(0, -104.25) * mm});
            skLineSegment(sketch, "E87.MirrorCS", {"start": v(-33, -74.25) * mm, "end": v(-15, -92.25) * mm});
            skLineSegment(sketch, "E88.MirrorCS", {"start": v(33, -74.25) * mm, "end": v(15, -92.25) * mm});
            skLineSegment(sketch, "E89.MirrorCS", {"start": v(-15, -104.25) * mm, "end": v(-15, -92.25) * mm});
            skArc(sketch, "E90.MirrorCS", {"start": v(15, -104.25) * mm, "mid": v(0, -119.25) * mm, "end": v(-15, -104.25) * mm});
            skLineSegment(sketch, "E91.MirrorCS", {"start": v(15, -104.25) * mm, "end": v(15, -92.25) * mm});
            skCircle(sketch, "E92.MirrorC", {"center": v(0, -104.25) * mm, "radius": 6 * mm});
            skSolve(sketch);
        }
        {
            var Q0;
            Q0=makeQuery(id+"F16.imprint","IMPRINT",FACE,{"disambiguationData":[TD([[makeQuery(id+"F16.imprint","IMPRINT",EDGE,{"derivedFrom":sQuery(id+"F16.wireOp",EDGE,"E80")}),-1.0]])]});
            var Q1;
            Q1=makeQuery(id+"F16.imprint","IMPRINT",FACE,{"disambiguationData":[TD([[makeQuery(id+"F16.imprint","IMPRINT",EDGE,{"derivedFrom":makeQuery(id+"F1.opExtrude","CAP_EDGE",EDGE,{"disambiguationData":[OSD([sQuery(id+"F0.wireOp",EDGE,"E1.left")])],"isStart":true})}),-1.0]])]});
            var Q2;
            {var subQ3=sQuery(id+"F16.wireOp",EDGE,"E87.MirrorCS");Q2=makeQuery(id+"F16.imprint","IMPRINT",FACE,{"disambiguationData":[TD([[makeQuery(id+"F16.imprint","IMPRINT",EDGE,{"derivedFrom":subQ3}),1.0]])]});}
            extrude(context, id + "F17", {"entities" : qUnion([Q0, Q1, Q2]), "depth" : 2 * mm});
        }
    });
